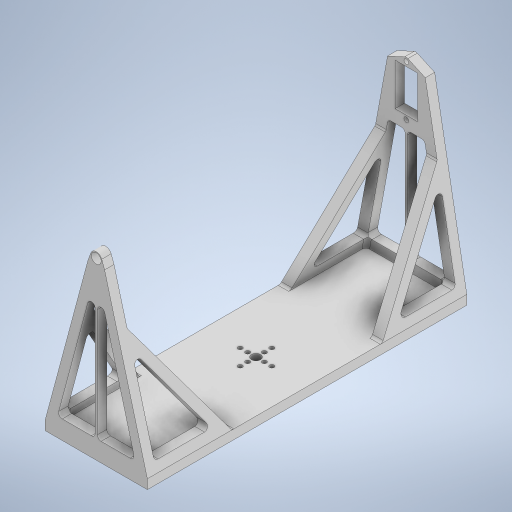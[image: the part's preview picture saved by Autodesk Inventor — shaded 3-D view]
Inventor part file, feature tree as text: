
AUTODESK INVENTOR PART (.ipt)
format: ipt  version: 2024 (Build 280153000, 153)  size: 654,336 bytes
history: native  units: mm
features: extrude x11, sketch x11, projected_geometry x9, fillet x5
ambient origin geometry x8: Origin, YZ Plane, XZ Plane, XY Plane, X Axis, Y Axis, Z Axis, Center Point
bodies: Solid1 (feature_tree)
feature tree (36):
  extrude  "Extrusion1"  TaperAngle=75.0deg  [1 undecoded]
  fillet  "Fillet1"  [1 undecoded]
  extrude  "Extrusion2"  Depth=5.2mm
  extrude  "Extrusion3"  Depth=12.217305mm
  extrude  "Extrusion6"  Depth=12.217305mm
  extrude  "Extrusion7"  Depth=5.0mm
  extrude  "Extrusion8"  Depth=5.0mm
  fillet  "Fillet2"  Radius=5.0mm
  extrude  "Extrusion9"  Depth=2.0mm
  extrude  "Extrusion10"  Depth=5.0mm TaperAngle=0.0deg
  extrude  "Extrusion11"  Depth=5.0mm TaperAngle=0.0deg
  extrude  "Extrusion13"  Depth=18.6mm
  fillet  "Fillet4"  Radius=12.0mm
  fillet  "Fillet5"  Radius=22.4mm
  fillet  "Fillet6"  Radius=2.5mm
  extrude  "Extrusion14"  Depth=10.0mm
  sketch  "Sketch1"  dims[d0=85.0mm d1=75.0deg d2=75.0deg]
  sketch  "Sketch2"  dims[d4=6.2mm d6=5.2mm]
  projected_geometry  "Projected Loop1"
  sketch  "Sketch5"  dims[d7=3.490659mm d8=12.217305mm]
  projected_geometry  "Projected Loop2"
  sketch  "Sketch9"  dims[d9=3.490659mm d10=12.217305mm]
  sketch  "Sketch10"  dims[d15=54.40588mm d22=5.0mm]
  projected_geometry  "Projected Loop6"
  sketch  "Sketch11"  dims[d27=5.0mm d28=5.0mm d29=5.0mm d30=0.0mm]
  projected_geometry  "Projected Loop7"
  sketch  "Sketch14"  dims[d31=2.0mm d32=144.177mm]
  projected_geometry  "Projected Loop8"
  sketch  "Sketch16"  dims[d34=21.0mm d35=5.0mm d36=0.0mm]
  projected_geometry  "Projected Loop10"
  sketch  "Sketch17"  dims[d37=5.0mm d38=5.0mm d39=0.0mm]
  projected_geometry  "Projected Loop11"
  sketch  "Sketch19"  dims[d54=8.2mm d55=18.6mm d56=12.0mm d57=22.4mm d58=2.5mm]
  projected_geometry  "Projected Loop13"
  sketch  "Sketch20"  dims[d59=2.3mm d60=4.0mm d62=4.0mm d63=13.904681mm d64=11.34464mm d65=11.34464mm d66=21.78644mm d67=4.0mm d68=10.0mm d69=0.0mm d70=22.4mm d71=26.8mm d72=10.0mm d73=0.0mm d74=41.373627mm d75=10.0mm d76=0.0mm d77=2.0mm d79=40.0mm d80=0.0mm d81=0.0mm d82=0.0mm d83=5.0mm d84=0.0mm d87=54.0mm d88=64.808492mm d89=59.0mm d90=59.0mm d91=5.0mm d92=40.0mm d93=0.0mm d99=5.0mm d100=5.0mm d101=0.0mm d102=0.0mm d103=2.0mm d104=2.0mm d105=2.0mm d108=8.9mm d110=4.45mm d111=4.45mm d112=4.45mm d119=10.0mm d120=0.0mm d121=8.9mm d122=4.8mm d94=0.5mm d95=0.872665mm]
  projected_geometry  "Projected Loop14"
note: 2 required parameter values undecoded (feature->parameter linkage not recoverable at this tier; creation-order binding heuristic only, values carry confidence <= 0.55)
